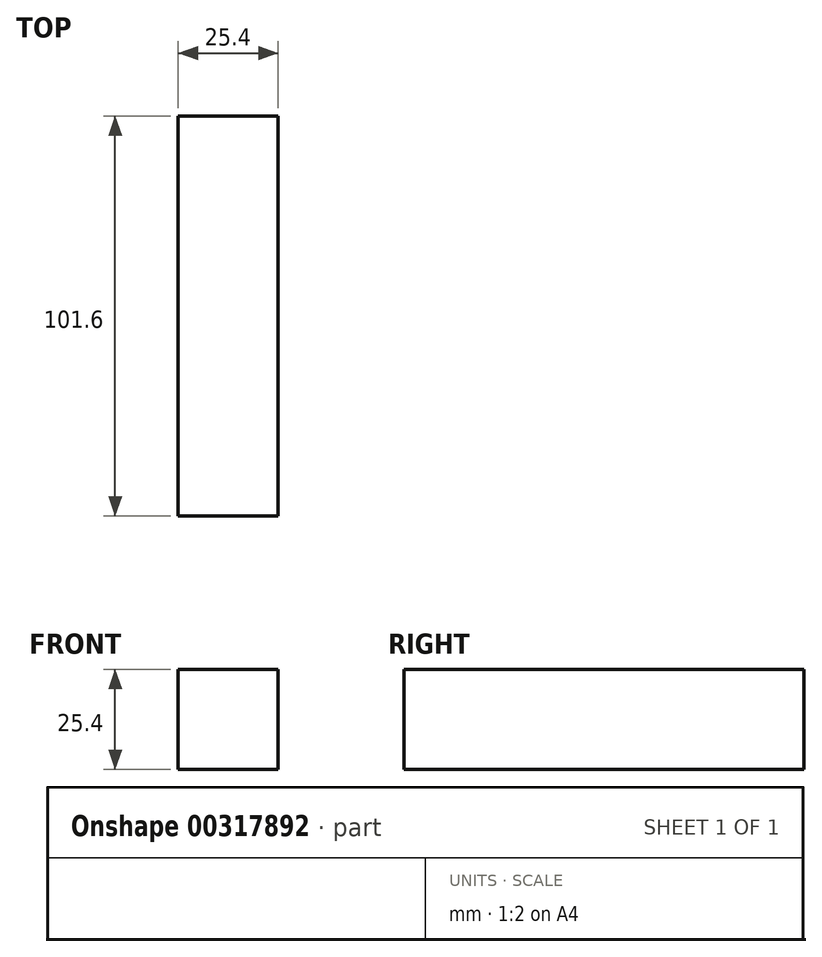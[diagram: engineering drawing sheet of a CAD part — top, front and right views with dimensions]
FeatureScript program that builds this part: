
annotation { "Feature Type Name" : "Feature", "Feature Type Description" : "" }
export const myFeature = defineFeature(function(context is Context, id is Id, definition is map)
    precondition{}
    {
        {
            var Q0;
            Q0=qCreatedBy(makeId("Front.planeOp"),FACE);
            var sketch = newSketch(context, id + "F0", { "sketchPlane" : qUnion([Q0])});
            skLineSegment(sketch, "E0.bottom", {"start": v(-8.03, 12.46) * mm, "end": v(17.37, 12.46) * mm});
            skLineSegment(sketch, "E0.top", {"start": v(-8.03, -12.94) * mm, "end": v(17.37, -12.94) * mm});
            skLineSegment(sketch, "E0.left", {"start": v(-8.03, 12.46) * mm, "end": v(-8.03, -12.94) * mm});
            skLineSegment(sketch, "E0.right", {"start": v(17.37, 12.46) * mm, "end": v(17.37, -12.94) * mm});
            skSolve(sketch);
        }
        {
            var Q0;
            Q0=makeQuery(id+"F0.imprint","IMPRINT",FACE,{"disambiguationData":[TD([[makeQuery(id+"F0.imprint","IMPRINT",EDGE,{"derivedFrom":sQuery(id+"F0.wireOp",EDGE,"E0.bottom")}),-1.0]])]});
            extrude(context, id + "F1", {"entities" : qUnion([Q0]), "depth" : 101.6 * mm});
        }
    });
